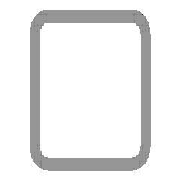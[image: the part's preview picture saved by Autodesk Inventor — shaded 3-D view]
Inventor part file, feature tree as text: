
AUTODESK INVENTOR PART (.ipt)
format: ipt  version: 2021 (Build 250183000, 183)  size: 130,048 bytes
history: native  units: mm (DEFAULTED — no unit token found)
features: other x4, sketch x3, extrude x1, plane x1
ambient origin geometry x8: Origin, YZ Plane, XZ Plane, XY Plane, X Axis, Y Axis, Z Axis, Center Point
bodies: Solid1 (feature_tree)
feature tree (9):
  parser-record x1  (decoder bookkeeping rows leaked as tree rows — omitted from the tree; the rows remain in map.json)
  other  "Driven Length"
  other  "Plano inicial"
  other  "Plano final"
  extrude  "Corpo"  TaperAngle=0.0deg  [1 undecoded]
  sketch  "Esboço"  dims[d11=50.8mm d12=4.7625mm d13=-0.0mm d14=2236.067977mm d15=25.4mm d16=25.4mm d17=9.525mm d18=90.0deg d19=2236.067977mm]
  sketch  "Sketch3"  dims[d3=2236.067977mm d4=0.0mm]
  plane  "Work Plane3"
  sketch  "Sketch4"  dims[d10=50.8mm]
note: 1 required parameter value undecoded (feature->parameter linkage not recoverable at this tier; creation-order binding heuristic only, values carry confidence <= 0.55)
